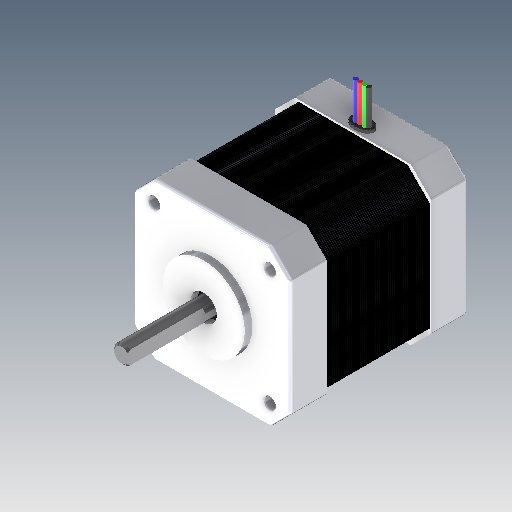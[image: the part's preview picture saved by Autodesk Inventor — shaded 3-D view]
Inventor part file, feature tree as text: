
AUTODESK INVENTOR PART (.ipt)
format: ipt  version: 2017 (Build 210142000, 142)  size: 1,190,400 bytes
history: native  units: mm
features: extrude x13, sketch x5, hole x4, fillet x4, chamfer x2, plane x1, pattern_linear x1, projected_geometry x1
ambient origin geometry x8: Origin, YZ Plane, XZ Plane, XY Plane, X Axis, Y Axis, Z Axis, Center Point
bodies: Solid1 (feature_tree)
feature tree (31):
  sketch  "Sketch1"  dims[d0=7.0mm d1=22.0mm]
  extrude  "Extrusion1"  Depth=22.0mm
  extrude  "Extrusion2"  Depth=31.0mm
  extrude  "Extrusion3"  Depth=3.0mm
  plane  "Work Plane2"
  extrude  "Extrusion7"  Depth=3.0mm
  extrude  "Extrusion8"  Depth=10.0mm
  chamfer  "Chamfer1"  Distance=42.0mm
  pattern_linear  "Rectangular Pattern2"  Spacing1=135.0deg  [1 undecoded]
  hole  "Hole1"  [1 undecoded]
  hole  "Hole2"  [1 undecoded]
  hole  "Hole3"  [1 undecoded]
  hole  "Hole4"  [1 undecoded]
  extrude  "Extrusion9"  Depth=10.0mm TaperAngle=0.0deg
  fillet  "Fillet1"  Radius=2.0mm
  fillet  "Fillet2"  Radius=48.0mm
  chamfer  "Chamfer2"  [1 undecoded]
  fillet  "Fillet3"  Radius=28.0mm
  sketch  "Sketch6"  dims[d10=3.0mm d11=3.0mm]
  extrude  "Extrusion10"  Depth=10.0mm
  fillet  "Fillet4"  Radius=1.0mm
  extrude  "Extrusion11"  Depth=10.0mm
  extrude  "Extrusion12"  Depth=10.0mm
  extrude  "Extrusion13"  Depth=10.0mm
  extrude  "Extrusion14"  Depth=10.0mm
  extrude  "Extrusion15"  Depth=10.0mm
  extrude  "Extrusion16"  Depth=10.0mm
  sketch  "Sketch4"  dims[d4=5.0mm d5=31.0mm]
  projected_geometry  "Projected Loop2"
  sketch  "Sketch5"  dims[d6=31.0mm d9=3.0mm]
  sketch  "Sketch11"  dims[d12=3.0mm d39=42.0mm d40=42.0mm d41=135.0deg d42=51.618795mm d43=51.618795mm d44=25.809398mm d45=25.809398mm d46=24.0mm d47=0.0mm d48=2.0mm d49=0.0mm d50=48.0mm d51=0.0mm d60=-10.0mm d126=28.0mm d127=0.0mm d128=1.0mm d129=1.0mm d130=1.0mm d131=1.0mm d132=0.5mm d134=0.5mm d135=0.5mm d136=0.5mm d137=0.5mm d138=1.0mm d139=1.0mm d140=0.5mm d141=0.0mm d145=0.125mm d146=2.0mm d147=45.0deg d148=560.0mm d150=0.5mm d151=10.0mm d152=10.0mm d153=6.0mm d154=6.0mm d155=4.0mm d156=2.0mm d157=90.0deg d158=3.0mm d159=0.0mm d160=10.0mm d161=10.0mm d162=6.0mm d163=6.0mm d164=4.0mm d165=2.0mm d166=90.0deg d167=3.0mm d168=0.0mm d169=10.0mm d170=10.0mm d171=6.0mm d172=6.0mm d173=4.0mm d174=2.0mm d175=90.0deg d176=3.0mm d177=0.0mm d178=10.0mm d179=10.0mm d180=6.0mm d181=6.0mm d182=4.0mm d183=2.0mm d184=90.0deg d185=3.0mm d186=0.0mm d187=48.0mm d188=0.0mm d189=47.0mm d190=0.0mm d191=1.0mm d192=1.0mm d193=0.5mm d194=2.0mm d195=45.0deg d196=0.5mm d197=1.2mm d198=40.0mm d200=1.2mm d201=10.0mm d203=10.0mm d205=2.5mm d206=2.5mm d207=1.0mm d208=0.0mm d209=0.3mm d210=10.0mm d211=0.0mm d212=10.0mm d213=0.0mm d214=10.0mm d215=0.0mm d216=10.0mm d217=0.0mm d218=0.2mm d219=5.0mm d220=0.0mm d221=0.0mm d225=20.0mm d226=0.0mm]
note: 6 required parameter values undecoded (feature->parameter linkage not recoverable at this tier; creation-order binding heuristic only, values carry confidence <= 0.55)
